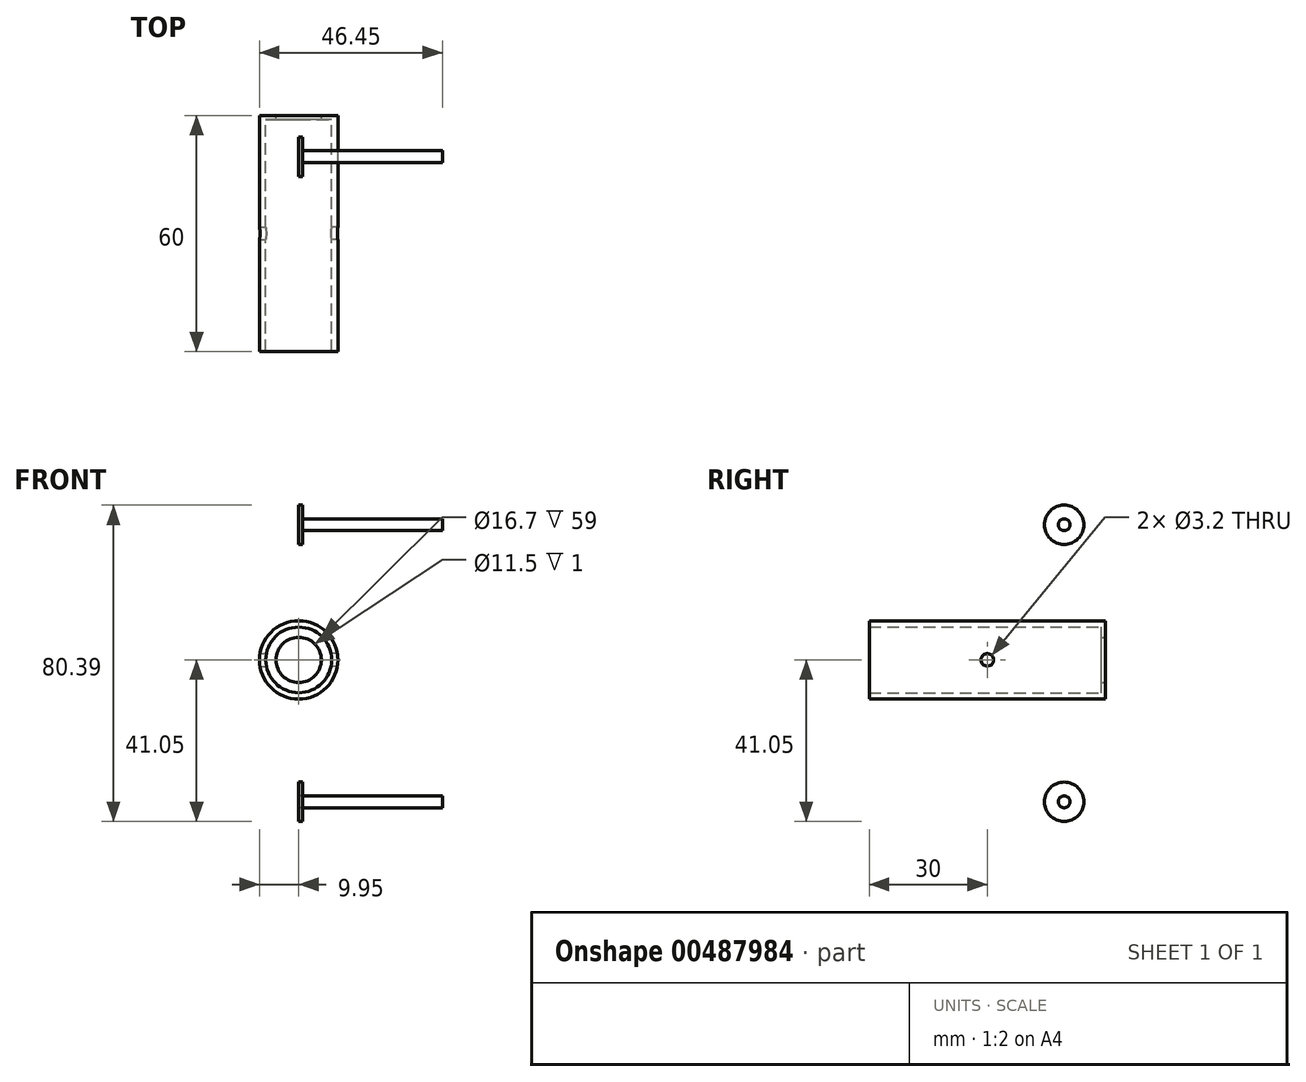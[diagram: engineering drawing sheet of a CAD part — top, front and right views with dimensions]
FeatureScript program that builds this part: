
annotation { "Feature Type Name" : "Feature", "Feature Type Description" : "" }
export const myFeature = defineFeature(function(context is Context, id is Id, definition is map)
    precondition{}
    {
        {
            var Q0;
            Q0=qCreatedBy(makeId("Front.planeOp"),FACE);
            var sketch = newSketch(context, id + "F0", { "sketchPlane" : qUnion([Q0])});
            skCircle(sketch, "E0", {"center": v(0, 0) * mm, "radius": 9.95 * mm});
            skCircle(sketch, "E1", {"center": v(0, 0) * mm, "radius": 8.35 * mm});
            skCircle(sketch, "E2", {"center": v(0, 0) * mm, "radius": 5.75 * mm});
            skSolve(sketch);
        }
        {
            var Q0;
            Q0=makeQuery(id+"F0.imprint","IMPRINT",FACE,{"disambiguationData":[TD([[makeQuery(id+"F0.imprint","IMPRINT",EDGE,{"derivedFrom":sQuery(id+"F0.wireOp",EDGE,"E0")}),1.0]])]});
            extrude(context, id + "F1", {"entities" : qUnion([Q0]), "depth" : 60 * mm});
        }
        {
            var Q0;
            Q0=makeQuery(id+"F0.imprint","IMPRINT",FACE,{"disambiguationData":[TD([[makeQuery(id+"F0.imprint","IMPRINT",EDGE,{"derivedFrom":sQuery(id+"F0.wireOp",EDGE,"E1")}),1.0]])]});
            extrude(context, id + "F2", {"entities" : qUnion([Q0]), "operationType" : NewBodyOperationType.ADD, "depth" : 1 * mm, "offsetDistance" : 25 * mm});
        }
        {
            var Q0;
            Q0=qCreatedBy(makeId("Right.planeOp"),FACE);
            var sketch = newSketch(context, id + "F3", { "sketchPlane" : qUnion([Q0])});
            skCircle(sketch, "E3", {"center": v(-30, 0) * mm, "radius": 1.6 * mm});
            skSolve(sketch);
        }
        {
            var Q0;
            Q0 = qSketchRegion(id + "F3", true);
            extrude(context, id + "F4", {"entities" : qUnion([Q0]), "operationType" : NewBodyOperationType.REMOVE, "endBound" : BoundingType.THROUGH_ALL, "oppositeDirection" : true, "depth" : 12 * mm});
        }
        {
            var Q0;
            Q0=qCreatedBy(makeId("Right.planeOp"),FACE);
            var sketch = newSketch(context, id + "F5", { "sketchPlane" : qUnion([Q0])});
            skCircle(sketch, "E4", {"center": v(-30, 0) * mm, "radius": 1.6 * mm});
            skSolve(sketch);
        }
        {
            var Q0;
            Q0=makeQuery(id+"F5.imprint","IMPRINT",FACE,{"disambiguationData":[TD([[makeQuery(id+"F5.imprint","IMPRINT",EDGE,{"derivedFrom":sQuery(id+"F5.wireOp",EDGE,"E4")}),1.0]])]});
            extrude(context, id + "F6", {"entities" : qUnion([Q0]), "operationType" : NewBodyOperationType.REMOVE, "endBound" : BoundingType.THROUGH_ALL, "depth" : 25 * mm});
        }
        {
            var Q0;
            Q0=qCreatedBy(makeId("Right.planeOp"),FACE);
            var sketch = newSketch(context, id + "F7", { "sketchPlane" : qUnion([Q0])});
            skCircle(sketch, "E5", {"center": v(-10.47, -36.05) * mm, "radius": 5 * mm});
            skCircle(sketch, "E6", {"center": v(-10.47, -36.05) * mm, "radius": 1.5 * mm});
            skSolve(sketch);
        }
        {
            var Q0;
            Q0=makeQuery(id+"F7.imprint","IMPRINT",FACE,{"disambiguationData":[TD([[makeQuery(id+"F7.imprint","IMPRINT",EDGE,{"derivedFrom":sQuery(id+"F7.wireOp",EDGE,"E5")}),1.0]])]});
            var Q1;
            Q1=makeQuery(id+"F7.imprint","IMPRINT",FACE,{"disambiguationData":[TD([[makeQuery(id+"F7.imprint","IMPRINT",EDGE,{"derivedFrom":sQuery(id+"F7.wireOp",EDGE,"E6")}),1.0]])]});
            extrude(context, id + "F8", {"entities" : qUnion([Q0, Q1]), "depth" : 1 * mm});
        }
        {
            var Q0;
            Q0=makeQuery(id+"F7.imprint","IMPRINT",FACE,{"disambiguationData":[TD([[makeQuery(id+"F7.imprint","IMPRINT",EDGE,{"derivedFrom":sQuery(id+"F7.wireOp",EDGE,"E6")}),1.0]])]});
            var Q1;
            Q1=sQuery(id+"F7.wireOp",EDGE,"E6");
            extrude(context, id + "F9", {"entities" : qUnion([Q0]), "surfaceEntities" : qUnion([Q1]), "depth" : 36.5 * mm, "offsetDistance" : 25 * mm});
        }
        {
            var Q0;
            Q0=qCreatedBy(makeId("Right.planeOp"),FACE);
            var sketch = newSketch(context, id + "F10", { "sketchPlane" : qUnion([Q0])});
            skCircle(sketch, "E7", {"center": v(-10.47, 34.34) * mm, "radius": 5 * mm});
            skCircle(sketch, "E8", {"center": v(-10.47, 34.34) * mm, "radius": 1.5 * mm});
            skSolve(sketch);
        }
        {
            var Q0;
            Q0=makeQuery(id+"F10.imprint","IMPRINT",FACE,{"disambiguationData":[TD([[makeQuery(id+"F10.imprint","IMPRINT",EDGE,{"derivedFrom":sQuery(id+"F10.wireOp",EDGE,"E8")}),1.0]])]});
            extrude(context, id + "F11", {"entities" : qUnion([Q0]), "depth" : 36.5 * mm, "offsetDistance" : 25 * mm});
        }
        {
            var Q0;
            Q0=makeQuery(id+"F10.imprint","IMPRINT",FACE,{"disambiguationData":[TD([[makeQuery(id+"F10.imprint","IMPRINT",EDGE,{"derivedFrom":sQuery(id+"F10.wireOp",EDGE,"E7")}),1.0]])]});
            extrude(context, id + "F12", {"entities" : qUnion([Q0]), "operationType" : NewBodyOperationType.ADD, "depth" : 1 * mm, "offsetDistance" : 25 * mm});
        }
    });
